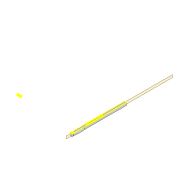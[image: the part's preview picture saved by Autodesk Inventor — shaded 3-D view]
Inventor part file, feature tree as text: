
AUTODESK INVENTOR PART (.ipt)
format: ipt  version: 2022 (Build 260153000, 153)  size: 134,144 bytes
history: native  units: mm
features: sketch x4, extrude x2, projected_geometry x2
ambient origin geometry x8: Origin, YZ Plane, XZ Plane, XY Plane, X Axis, Y Axis, Z Axis, Center Point
bodies: Solid1 (feature_tree)
feature tree (8):
  extrude  "Extrusion1"  Depth=8.0mm
  sketch  "Sketch2"  dims[d2=3.0mm d3=3.0mm]
  extrude  "Extrusion2"  Depth=3.0mm
  sketch  "Sketch4"  dims[d12=3.0mm d13=50.8mm d14=100.0mm d15=40.0mm d16=200.0mm d17=200.0mm d18=20.0mm d19=0.0mm d20=0.5mm d21=0.872665mm]
  sketch  "Sketch1"  dims[d0=319.927mm d1=8.0mm]
  projected_geometry  "Projected Loop1"
  sketch  "Sketch3"  dims[d4=8.0mm d5=0.0mm]
  projected_geometry  "Projected Loop2"
